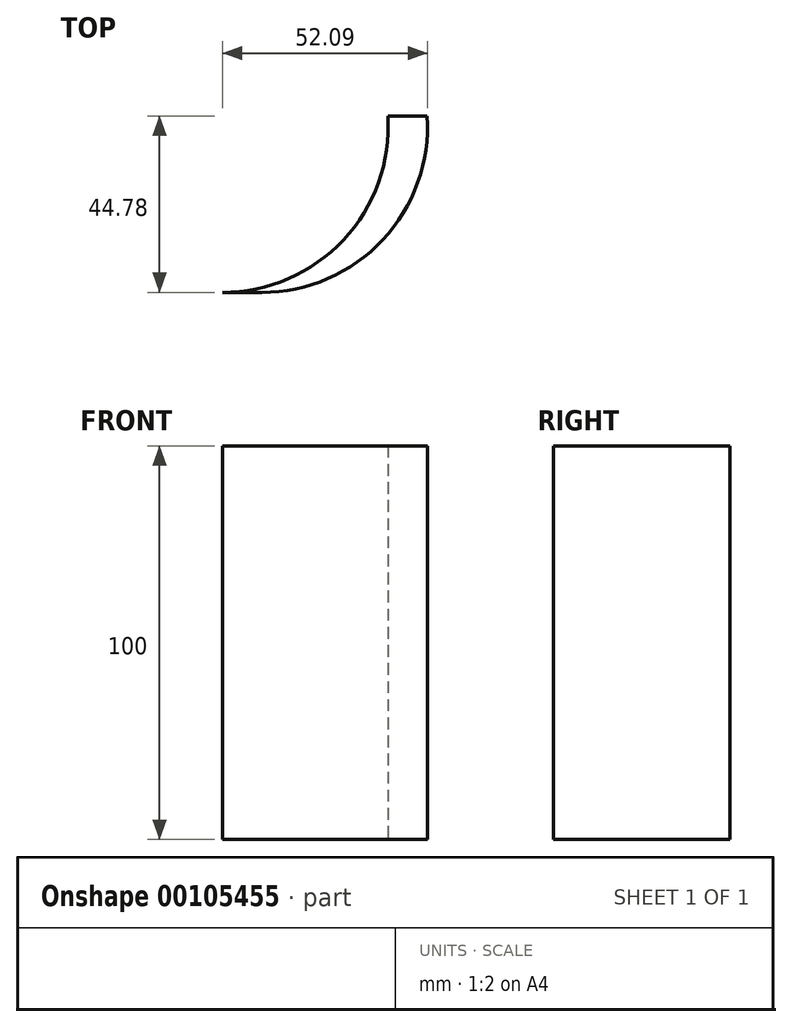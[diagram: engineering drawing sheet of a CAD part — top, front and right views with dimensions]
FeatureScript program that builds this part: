
annotation { "Feature Type Name" : "Feature", "Feature Type Description" : "" }
export const myFeature = defineFeature(function(context is Context, id is Id, definition is map)
    precondition{}
    {
        {
            var Q0;
            Q0=qCreatedBy(makeId("Top.planeOp"),FACE);
            var sketch = newSketch(context, id + "F0", { "sketchPlane" : qUnion([Q0])});
            skLineSegment(sketch, "E0", {"start": v(-42, -44.78) * mm, "end": v(-32, -44.78) * mm});
            skLineSegment(sketch, "E1", {"start": v(10, 0) * mm, "end": v(0, 0) * mm});
            skArc(sketch, "E2", {"start": v(-42, -44.78) * mm, "mid": v(-11.3, -31.48) * mm, "end": v(0, 0) * mm});
            skArc(sketch, "E3", {"start": v(-32, -44.78) * mm, "mid": v(-1.3, -31.48) * mm, "end": v(10, 0) * mm});
            skSolve(sketch);
        }
        {
            var Q0;
            Q0=makeQuery(id+"F0.imprint","IMPRINT",FACE,{"disambiguationData":[TD([[makeQuery(id+"F0.imprint","IMPRINT",EDGE,{"derivedFrom":sQuery(id+"F0.wireOp",EDGE,"E0")}),1.0]])]});
            extrude(context, id + "F1", {"entities" : qUnion([Q0]), "depth" : 100 * mm});
        }
    });
